# Revit family: 12593SGP_NEW
name_source: partatom
category: Plumbing Fixtures
revit_build: Autodesk Revit 2018 (Build: 20170223_1515(x64)
units: mm (PartAtom-declared; Revit-internal decimal feet)

## family parameters
Cut with Voids When Loaded = Yes
Host = Face
OmniClass Number = 23.31.17.00
OmniClass Title = Showers
Part Type = Normal
Room Calculation Point = No
Round Connector Dimension = Use Diameter
Shared = No

## types (2) — shared parameters
BIMobject category = Showers
Default Elevation = 1219 mm
Description = AXOR Starck Shower module 110/220 1jet 2 ticks with shoulder shower
Design country = Germany
Edition number = 1
IFC Classification = Sanitary Terminal
Manufacturer = AXOR
Manufacturer country = Germany
Manufacturer name = AXOR
Masterformat 2014 Code = 22 41 23
Masterformat 2014 Description = Residential Showers
Model = 12593SGP
OmniClass Code = 23-31 17 00
OmniClass Description = Showers
Product Guid = e416eb90-53d7-42c8-bc63-8db3e0131940
Product SKU = 12593SGP
Product data url = https://bimobject.com
Product name = AXOR Starck Shower module 110/220 1jet 2 ticks with shoulder shower
Product url = https://www.axor-design.com
QR code = https://bimobject.com
UNSPSC Code = 30181503
URL = https://www.axor-design.com
Uniclass 2015 Code = Pr_40_20_87_76
Uniclass 2015 Name = Shower heads
Uniformat II Code = D2010
Uniformat II Description = Plumbing Fixtures
zero-valued in all types: Version

## per-type parameters (varying)
| type | Material 1 |
| 009 Chrome | AXOR - Metal - 009 Chrome |
| 679 Matte Black | AXOR - Metal - 679 Matte Black |

## geometry (parser evidence)
native form markers: Sweep x2
no freeform markers — native parametric forms only
